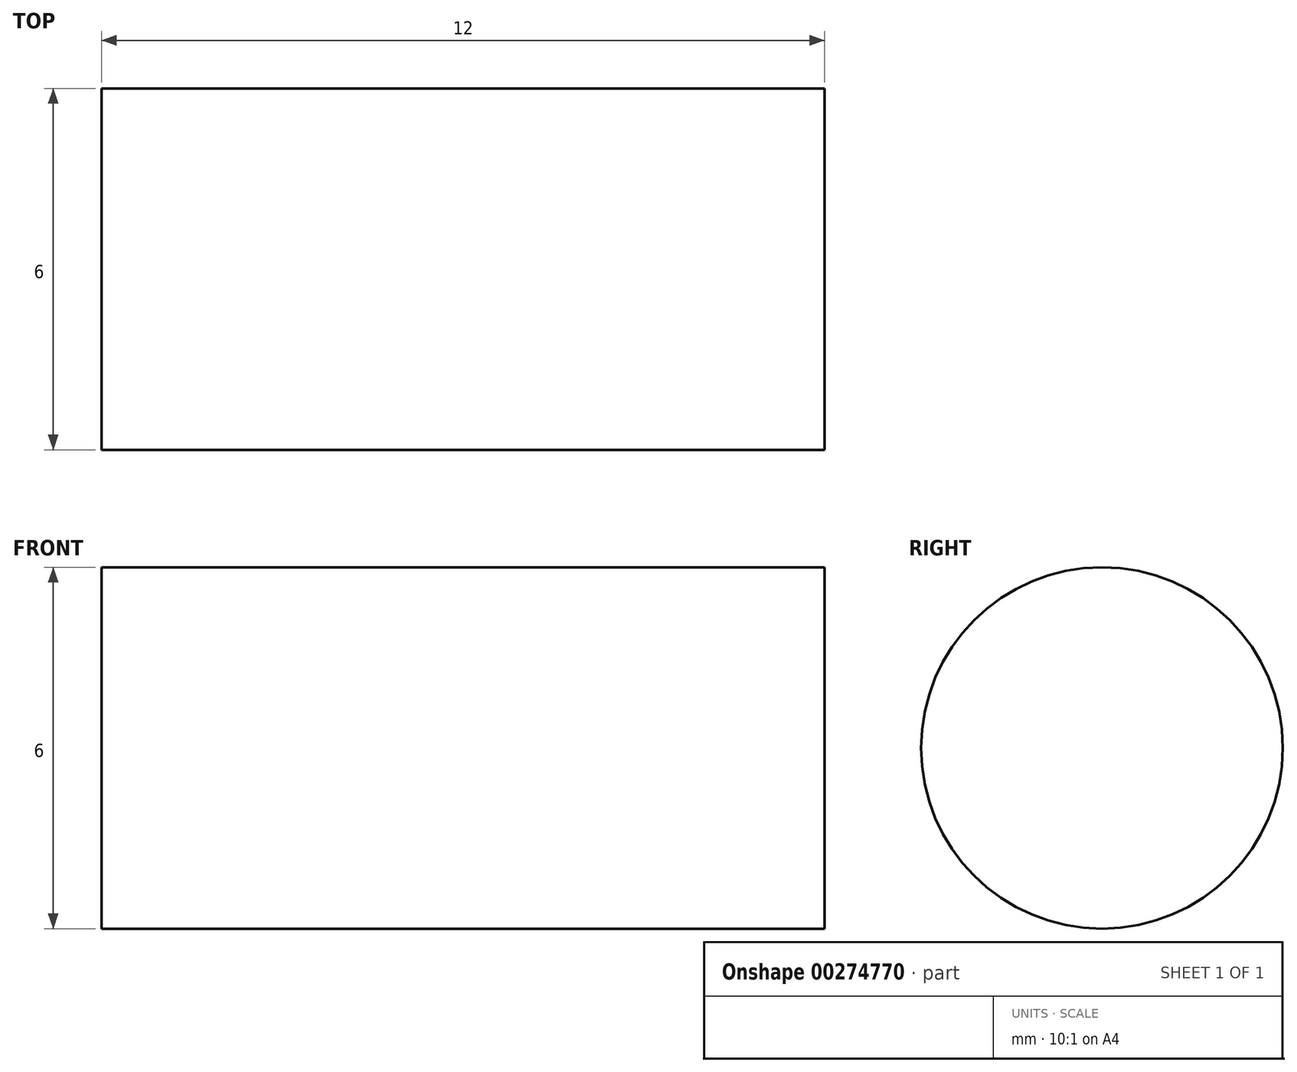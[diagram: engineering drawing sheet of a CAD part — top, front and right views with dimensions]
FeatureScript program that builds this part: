
annotation { "Feature Type Name" : "Feature", "Feature Type Description" : "" }
export const myFeature = defineFeature(function(context is Context, id is Id, definition is map)
    precondition{}
    {
        {
            var Q0;
            Q0=qCreatedBy(makeId("Front.planeOp"),FACE);
            var sketch = newSketch(context, id + "F0", { "sketchPlane" : qUnion([Q0])});
            skLineSegment(sketch, "E0.bottom", {"start": v(0, 0) * mm, "end": v(12, 0) * mm});
            skLineSegment(sketch, "E0.top", {"start": v(0, 3) * mm, "end": v(12, 3) * mm});
            skLineSegment(sketch, "E0.left", {"start": v(0, 0) * mm, "end": v(0, 3) * mm});
            skLineSegment(sketch, "E0.right", {"start": v(12, 0) * mm, "end": v(12, 3) * mm});
            skSolve(sketch);
        }
        {
            var Q0;
            Q0=makeQuery(id+"F0.imprint","IMPRINT",FACE,{"disambiguationData":[TD([[makeQuery(id+"F0.imprint","IMPRINT",EDGE,{"derivedFrom":sQuery(id+"F0.wireOp",EDGE,"E0.bottom")}),1.0]])]});
            var Q1;
            Q1=sQuery(id+"F0.wireOp",EDGE,"E0.bottom");
            revolve(context, id + "F1", {"entities" : qUnion([Q0]), "axis" : qUnion([Q1]), "revolveType" : RevolveType.FULL});
        }
    });
